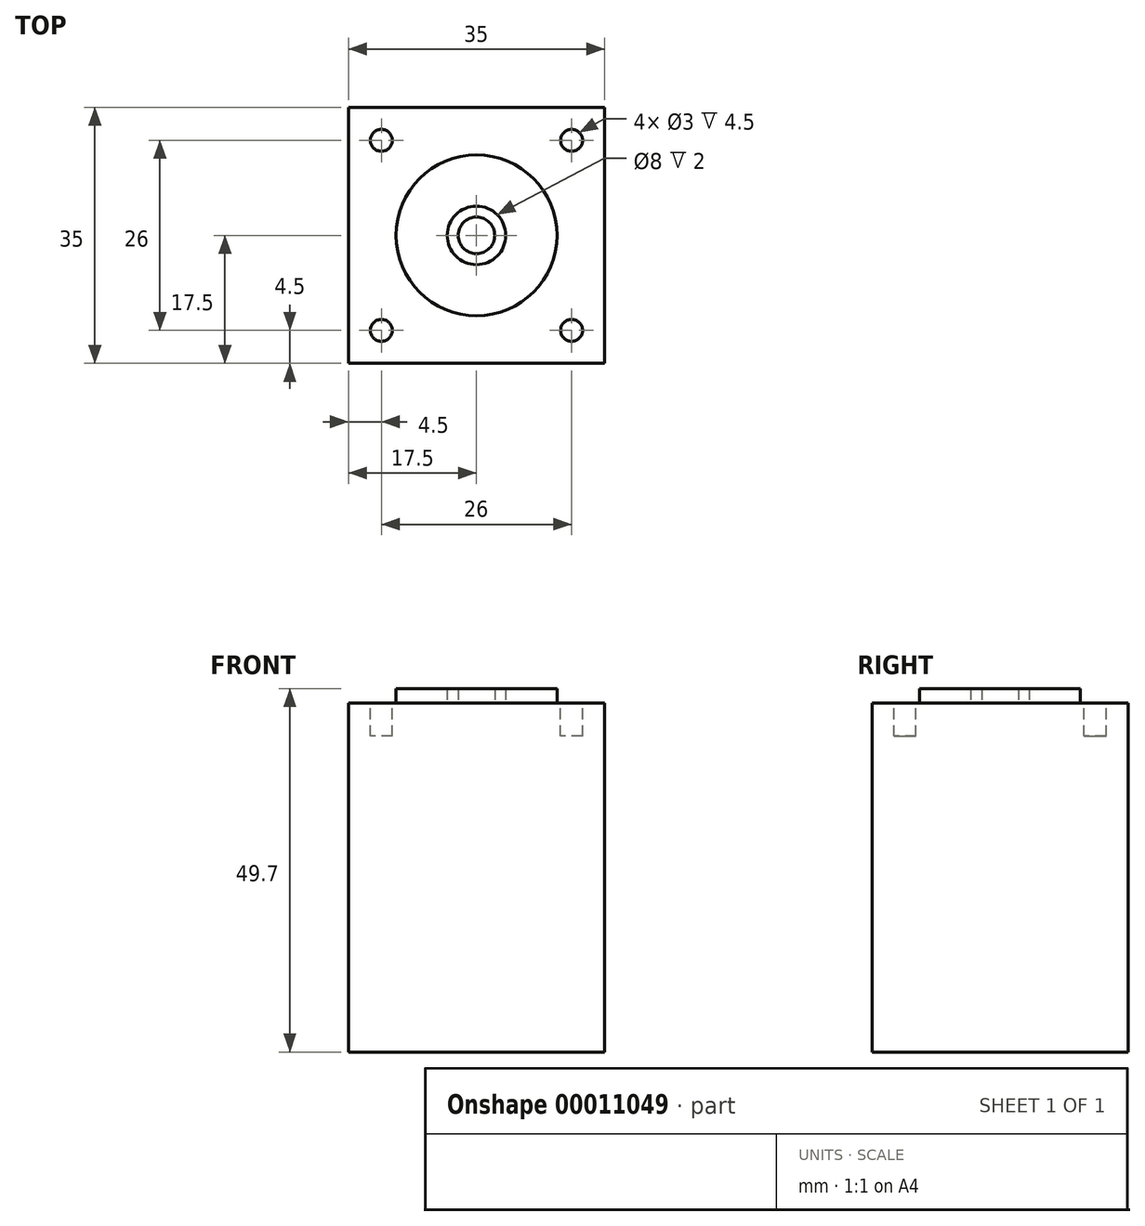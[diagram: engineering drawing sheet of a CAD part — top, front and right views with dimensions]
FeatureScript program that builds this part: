
annotation { "Feature Type Name" : "Feature", "Feature Type Description" : "" }
export const myFeature = defineFeature(function(context is Context, id is Id, definition is map)
    precondition{}
    {
        {
            var Q0;
            Q0=qCreatedBy(makeId("Top.planeOp"),FACE);
            var sketch = newSketch(context, id + "F0", { "sketchPlane" : qUnion([Q0])});
            skLineSegment(sketch, "E0.bottom", {"start": v(-17.5, 17.5) * mm, "end": v(17.5, 17.5) * mm});
            skLineSegment(sketch, "E0.top", {"start": v(-17.5, -17.5) * mm, "end": v(17.5, -17.5) * mm});
            skLineSegment(sketch, "E0.left", {"start": v(-17.5, 17.5) * mm, "end": v(-17.5, -17.5) * mm});
            skLineSegment(sketch, "E0.right", {"start": v(17.5, 17.5) * mm, "end": v(17.5, -17.5) * mm});
            skLineSegment(sketch, "E1", {"start": v(-17.5, 17.5) * mm, "end": v(17.5, -17.5) * mm, "construction": true});
            skLineSegment(sketch, "E2", {"start": v(17.5, 17.5) * mm, "end": v(-17.5, -17.5) * mm, "construction": true});
            skPoint(sketch, "E3", {"position": v(0, 0) * mm});
            skCircle(sketch, "E4", {"center": v(-13, 13) * mm, "radius": 1.5 * mm});
            skCircle(sketch, "E5", {"center": v(13, 13) * mm, "radius": 1.5 * mm});
            skCircle(sketch, "E6", {"center": v(-13, -13) * mm, "radius": 1.5 * mm});
            skCircle(sketch, "E7", {"center": v(13, -13) * mm, "radius": 1.5 * mm});
            skCircle(sketch, "E8", {"center": v(0, 0) * mm, "radius": 11 * mm});
            skCircle(sketch, "E9", {"center": v(0, 0) * mm, "radius": 4 * mm});
            skCircle(sketch, "E10", {"center": v(0, 0) * mm, "radius": 2.5 * mm});
            skSolve(sketch);
        }
        {
            var Q0;
            Q0=makeQuery(id+"F0.imprint","IMPRINT",FACE,{"disambiguationData":[TD([[makeQuery(id+"F0.imprint","IMPRINT",EDGE,{"derivedFrom":sQuery(id+"F0.wireOp",EDGE,"E4")}),1.0]])]});
            var Q1;
            Q1=makeQuery(id+"F0.imprint","IMPRINT",FACE,{"disambiguationData":[TD([[makeQuery(id+"F0.imprint","IMPRINT",EDGE,{"derivedFrom":sQuery(id+"F0.wireOp",EDGE,"E8")}),1.0]])]});
            var Q2;
            Q2=makeQuery(id+"F0.imprint","IMPRINT",FACE,{"disambiguationData":[TD([[makeQuery(id+"F0.imprint","IMPRINT",EDGE,{"derivedFrom":sQuery(id+"F0.wireOp",EDGE,"E10")}),1.0]])]});
            var Q3;
            Q3=makeQuery(id+"F0.imprint","IMPRINT",FACE,{"disambiguationData":[TD([[makeQuery(id+"F0.imprint","IMPRINT",EDGE,{"derivedFrom":sQuery(id+"F0.wireOp",EDGE,"E9")}),1.0]])]});
            var Q4;
            Q4=makeQuery(id+"F0.imprint","IMPRINT",FACE,{"disambiguationData":[TD([[makeQuery(id+"F0.imprint","IMPRINT",EDGE,{"derivedFrom":sQuery(id+"F0.wireOp",EDGE,"E6")}),1.0]])]});
            var Q5;
            Q5=makeQuery(id+"F0.imprint","IMPRINT",FACE,{"disambiguationData":[TD([[makeQuery(id+"F0.imprint","IMPRINT",EDGE,{"derivedFrom":sQuery(id+"F0.wireOp",EDGE,"E5")}),1.0]])]});
            var Q6;
            Q6=makeQuery(id+"F0.imprint","IMPRINT",FACE,{"disambiguationData":[TD([[makeQuery(id+"F0.imprint","IMPRINT",EDGE,{"derivedFrom":sQuery(id+"F0.wireOp",EDGE,"E7")}),1.0]])]});
            var Q7;
            Q7=makeQuery(id+"F0.imprint","IMPRINT",FACE,{"disambiguationData":[TD([[makeQuery(id+"F0.imprint","IMPRINT",EDGE,{"derivedFrom":sQuery(id+"F0.wireOp",EDGE,"E0.bottom")}),-1.0]])]});
            extrude(context, id + "F1", {"entities" : qUnion([Q0, Q1, Q2, Q3, Q4, Q5, Q6, Q7]), "oppositeDirection" : true, "depth" : 47.7 * mm});
        }
        {
            var Q0;
            Q0=makeQuery(id+"F0.imprint","IMPRINT",FACE,{"disambiguationData":[TD([[makeQuery(id+"F0.imprint","IMPRINT",EDGE,{"derivedFrom":sQuery(id+"F0.wireOp",EDGE,"E6")}),1.0]])]});
            var Q1;
            Q1=makeQuery(id+"F0.imprint","IMPRINT",FACE,{"disambiguationData":[TD([[makeQuery(id+"F0.imprint","IMPRINT",EDGE,{"derivedFrom":sQuery(id+"F0.wireOp",EDGE,"E4")}),1.0]])]});
            var Q2;
            Q2=makeQuery(id+"F0.imprint","IMPRINT",FACE,{"disambiguationData":[TD([[makeQuery(id+"F0.imprint","IMPRINT",EDGE,{"derivedFrom":sQuery(id+"F0.wireOp",EDGE,"E5")}),1.0]])]});
            var Q3;
            Q3=makeQuery(id+"F0.imprint","IMPRINT",FACE,{"disambiguationData":[TD([[makeQuery(id+"F0.imprint","IMPRINT",EDGE,{"derivedFrom":sQuery(id+"F0.wireOp",EDGE,"E7")}),1.0]])]});
            extrude(context, id + "F2", {"entities" : qUnion([Q0, Q1, Q2, Q3]), "operationType" : NewBodyOperationType.REMOVE, "oppositeDirection" : true, "depth" : 4.5 * mm});
        }
        {
            var Q0;
            Q0=makeQuery(id+"F0.imprint","IMPRINT",FACE,{"disambiguationData":[TD([[makeQuery(id+"F0.imprint","IMPRINT",EDGE,{"derivedFrom":sQuery(id+"F0.wireOp",EDGE,"E8")}),1.0]])]});
            var Q1;
            Q1=makeQuery(id+"F0.imprint","IMPRINT",FACE,{"disambiguationData":[TD([[makeQuery(id+"F0.imprint","IMPRINT",EDGE,{"derivedFrom":sQuery(id+"F0.wireOp",EDGE,"E10")}),1.0]])]});
            extrude(context, id + "F3", {"entities" : qUnion([Q0, Q1]), "operationType" : NewBodyOperationType.ADD, "depth" : 2 * mm});
        }
    });
